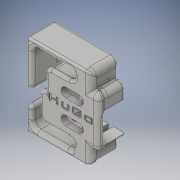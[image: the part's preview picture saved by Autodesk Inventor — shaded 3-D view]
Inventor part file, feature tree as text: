
AUTODESK INVENTOR PART (.ipt)
format: ipt  version: 2016 (Build 200138000, 138)  size: 864,256 bytes
history: native  units: in
note: dims shown in document units (in); Inventor stores cm internally (conversion verified against a paired STEP export)
features: sketch x21, other x3, plane x2
ambient origin geometry x8: Origin, YZ Plane, XZ Plane, XY Plane, X Axis, Y Axis, Z Axis, Center Point
bodies: Solid1 (feature_tree)
feature tree (26):
  other  "Hip_rotation_temp_MIR.ipt"
  other  "Solid1::Hip_rotation_temp_MIR.ipt"
  other  "TaggingFeature1"
  sketch  "Sketch1"  dims[d0=0.3937in]
  sketch  "Sketch12"
  sketch  "Sketch14"
  sketch  "Sketch17"
  sketch  "Sketch18"
  sketch  "Sketch20"
  sketch  "Sketch21"
  sketch  "Sketch22"
  sketch  "Sketch25"
  sketch  "Sketch26"
  sketch  "Sketch27"
  sketch  "Sketch13"
  sketch  "Sketch15"
  sketch  "Sketch16"
  sketch  "Sketch24"
  sketch  "Sketch28"
  sketch  "Sketch29"
  sketch  "Sketch31"
  sketch  "Sketch32"
  sketch  "Sketch34"
  sketch  "Sketch35"
  plane  "Work Plane1"
  plane  "Work Plane2"
